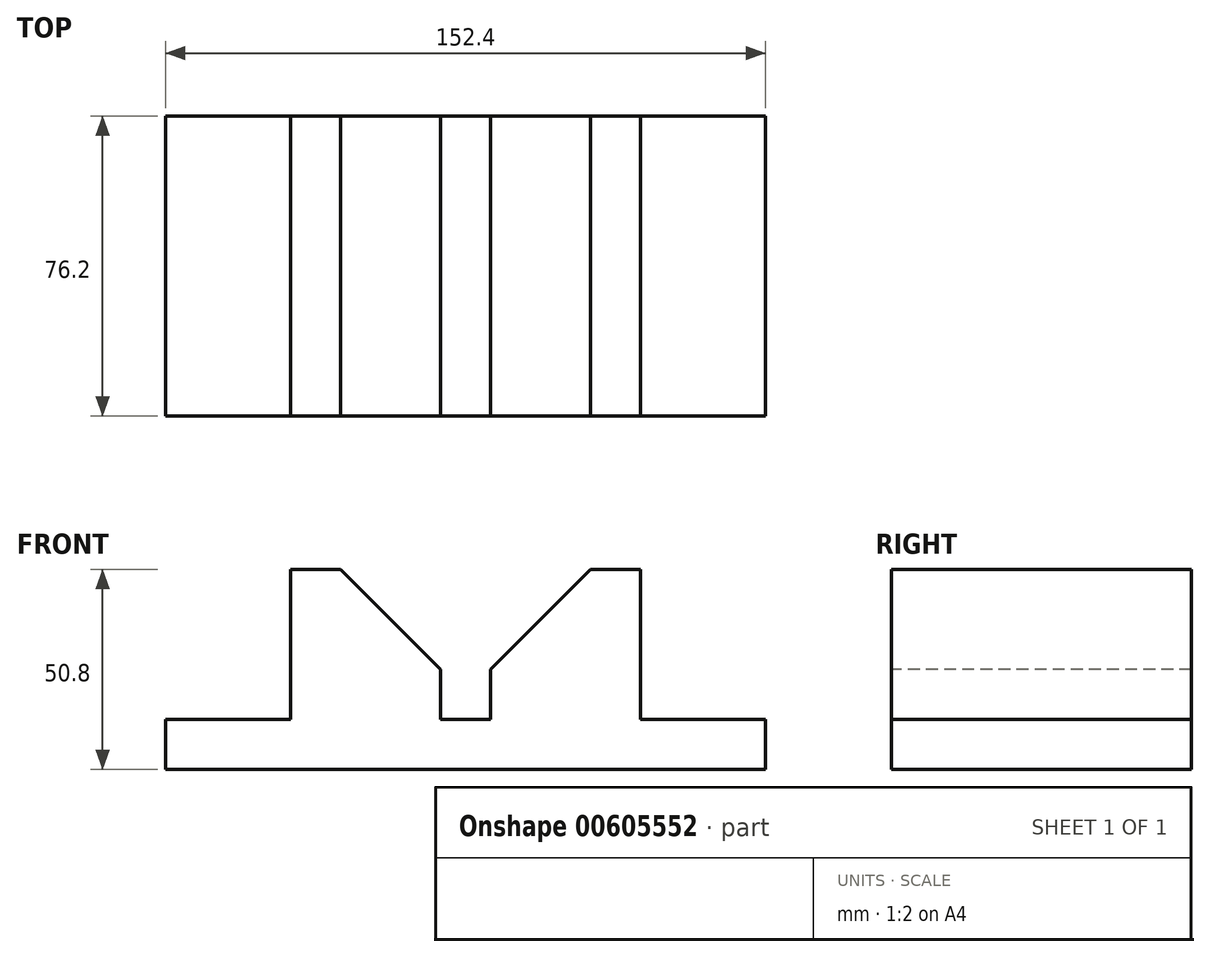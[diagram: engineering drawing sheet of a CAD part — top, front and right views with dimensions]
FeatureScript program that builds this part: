
annotation { "Feature Type Name" : "Feature", "Feature Type Description" : "" }
export const myFeature = defineFeature(function(context is Context, id is Id, definition is map)
    precondition{}
    {
        {
            var Q0;
            Q0=qCreatedBy(makeId("Front.planeOp"),FACE);
            var sketch = newSketch(context, id + "F0", { "sketchPlane" : qUnion([Q0])});
            skLineSegment(sketch, "E0", {"start": v(0, 0) * mm, "end": v(152.4, 0) * mm});
            skLineSegment(sketch, "E1", {"start": v(152.4, 0) * mm, "end": v(152.4, 12.7) * mm});
            skLineSegment(sketch, "E2", {"start": v(152.4, 12.7) * mm, "end": v(120.65, 12.7) * mm});
            skLineSegment(sketch, "E3", {"start": v(120.65, 12.7) * mm, "end": v(120.65, 50.8) * mm});
            skLineSegment(sketch, "E4", {"start": v(120.65, 50.8) * mm, "end": v(107.95, 50.8) * mm});
            skLineSegment(sketch, "E5", {"start": v(107.95, 50.8) * mm, "end": v(82.55, 25.4) * mm});
            skLineSegment(sketch, "E6", {"start": v(82.55, 25.4) * mm, "end": v(82.55, 12.7) * mm});
            skLineSegment(sketch, "E7", {"start": v(82.55, 12.7) * mm, "end": v(69.85, 12.7) * mm});
            skLineSegment(sketch, "E8", {"start": v(69.85, 12.7) * mm, "end": v(69.85, 25.4) * mm});
            skLineSegment(sketch, "E9", {"start": v(69.85, 25.4) * mm, "end": v(44.45, 50.8) * mm});
            skLineSegment(sketch, "E10", {"start": v(44.45, 50.8) * mm, "end": v(31.75, 50.8) * mm});
            skLineSegment(sketch, "E11", {"start": v(31.75, 50.8) * mm, "end": v(31.75, 12.7) * mm});
            skLineSegment(sketch, "E12", {"start": v(31.75, 12.7) * mm, "end": v(0, 12.7) * mm});
            skLineSegment(sketch, "E13", {"start": v(0, 12.7) * mm, "end": v(0, 0) * mm});
            skSolve(sketch);
        }
        {
            var Q0;
            {var subQ0=sQuery(id+"F0.wireOp",EDGE,"E1");Q0=makeQuery(id+"F0.imprint","IMPRINT",FACE,{"disambiguationData":[TD([[makeQuery(id+"F0.imprint","IMPRINT",EDGE,{"derivedFrom":subQ0}),1.0]])]});}
            extrude(context, id + "F1", {"entities" : qUnion([Q0]), "oppositeDirection" : true, "depth" : 76.2 * mm, "offsetDistance" : 25.4 * mm});
        }
    });
